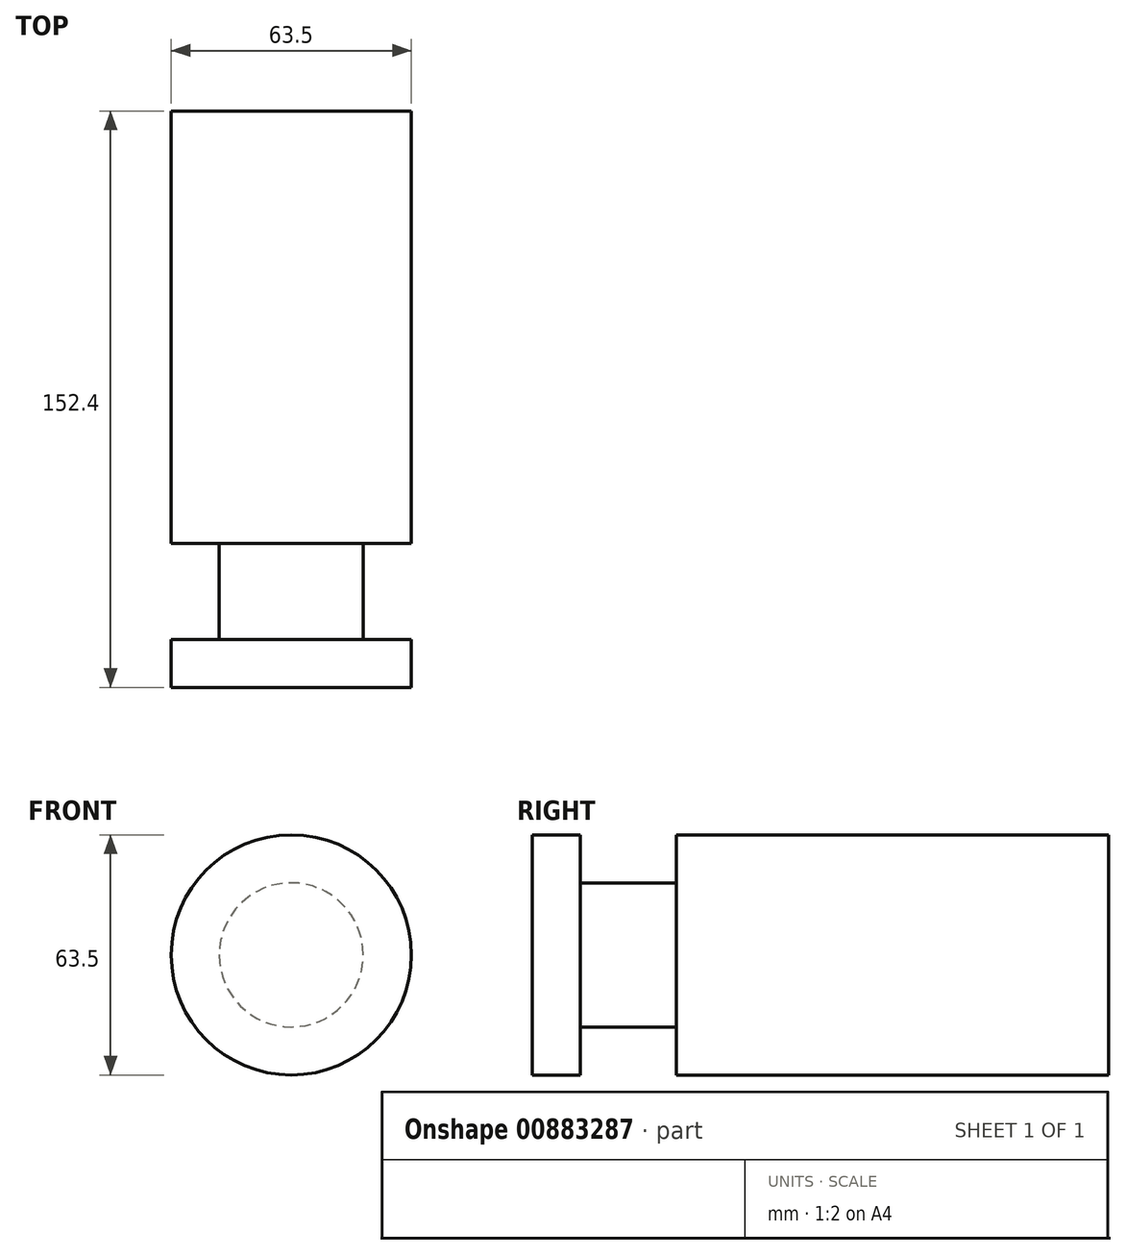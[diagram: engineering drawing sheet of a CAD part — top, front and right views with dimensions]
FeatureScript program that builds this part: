
annotation { "Feature Type Name" : "Feature", "Feature Type Description" : "" }
export const myFeature = defineFeature(function(context is Context, id is Id, definition is map)
    precondition{}
    {
        {
            var Q0;
            Q0=qCreatedBy(makeId("Front.planeOp"),FACE);
            var sketch = newSketch(context, id + "F0", { "sketchPlane" : qUnion([Q0])});
            skCircle(sketch, "E0", {"center": v(0, 0) * mm, "radius": 31.75 * mm});
            skSolve(sketch);
        }
        {
            var Q0;
            Q0=makeQuery(id+"F0.imprint","IMPRINT",FACE,{"disambiguationData":[TD([[makeQuery(id+"F0.imprint","IMPRINT",EDGE,{"derivedFrom":sQuery(id+"F0.wireOp",EDGE,"E0")}),1.0]])]});
            var Q1;
            Q1=sQuery(id+"F0.wireOp",EDGE,"E0");
            extrude(context, id + "F1", {"entities" : qUnion([Q0]), "surfaceEntities" : qUnion([Q1]), "oppositeDirection" : true, "depth" : 152.4 * mm, "offsetDistance" : 25.4 * mm});
        }
        {
            var Q0;
            Q0=qCreatedBy(makeId("Right.planeOp"),FACE);
            var sketch = newSketch(context, id + "F2", { "sketchPlane" : qUnion([Q0])});
            skLineSegment(sketch, "E1", {"start": v(0, -31.75) * mm, "end": v(152.4, -31.75) * mm});
            skLineSegment(sketch, "E2", {"start": v(152.4, 31.75) * mm, "end": v(0, 31.75) * mm});
            skLineSegment(sketch, "E3.bottom", {"start": v(12.7, 31.75) * mm, "end": v(38.1, 31.75) * mm});
            skLineSegment(sketch, "E3.top", {"start": v(12.7, 19.05) * mm, "end": v(38.1, 19.05) * mm});
            skLineSegment(sketch, "E3.left", {"start": v(12.7, 31.75) * mm, "end": v(12.7, 19.05) * mm});
            skLineSegment(sketch, "E3.right", {"start": v(38.1, 31.75) * mm, "end": v(38.1, 19.05) * mm});
            skLineSegment(sketch, "E4", {"start": v(0, 0) * mm, "end": v(153.08, 0) * mm, "construction": true});
            skSolve(sketch);
        }
        {
            var Q0;
            Q0 = qSketchRegion(id + "F2", true);
            var Q1;
            Q1 = qConstructionFilter(qBodyType(qCreatedBy(id + "F2" ,EDGE), BodyType.WIRE), ConstructionObject.NO);
            var Q2;
            Q2=sQuery(id+"F2.wireOp",EDGE,"E4");
            revolve(context, id + "F3", {"operationType" : NewBodyOperationType.REMOVE, "surfaceOperationType" : NewSurfaceOperationType.NEW, "entities" : qUnion([Q0]), "surfaceEntities" : qUnion([Q1]), "axis" : qUnion([Q2]), "revolveType" : RevolveType.FULL, "oppositeDirection" : true});
        }
    });
